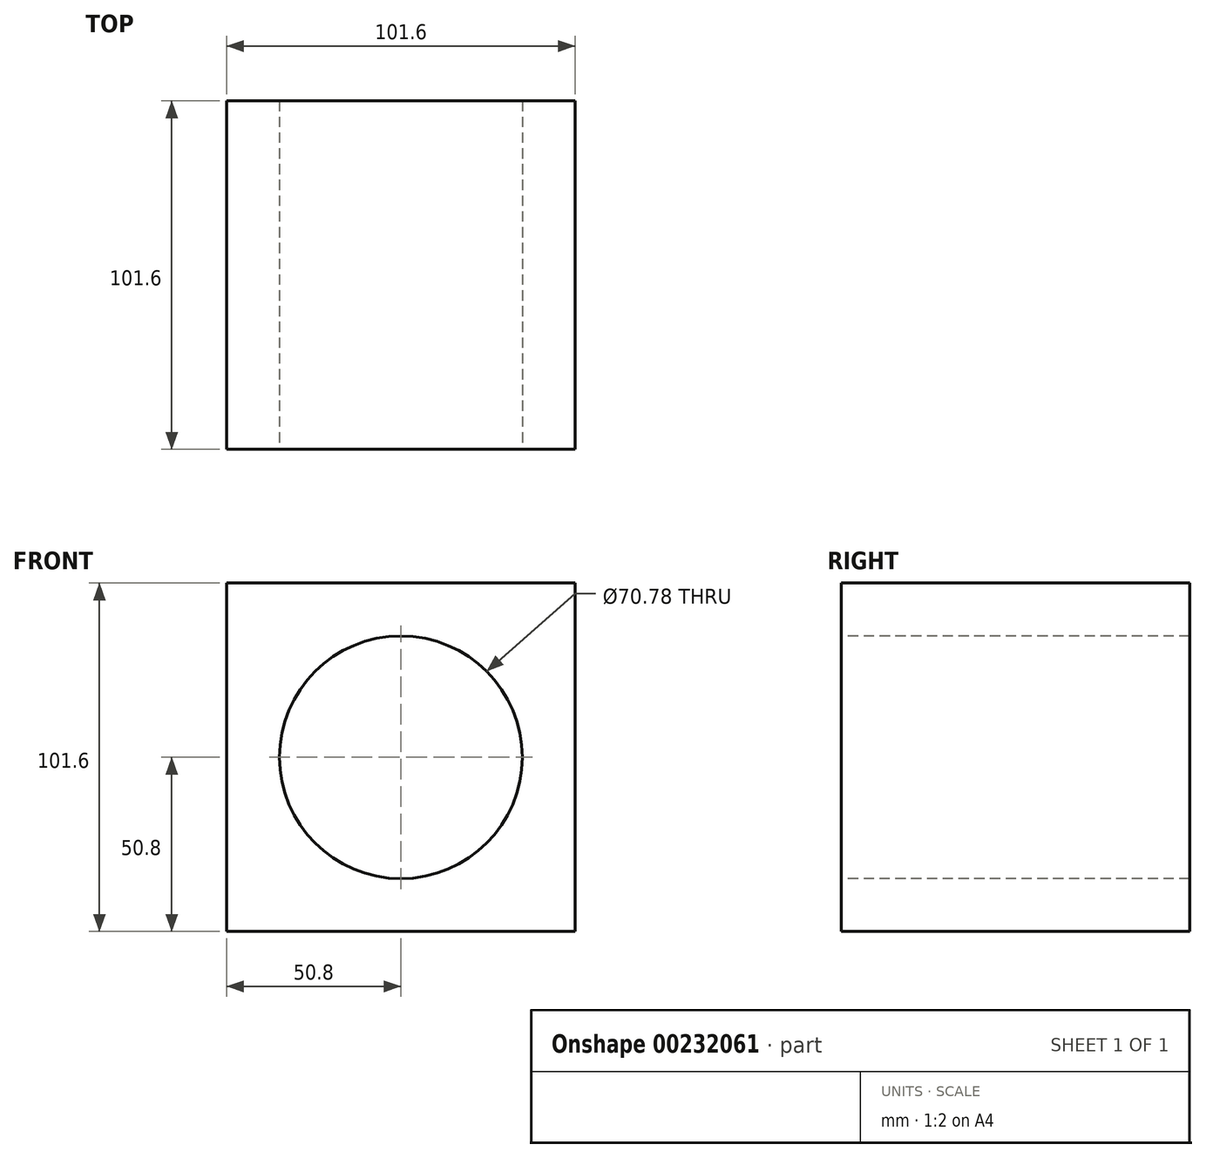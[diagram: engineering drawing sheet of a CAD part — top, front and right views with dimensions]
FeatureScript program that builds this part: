
annotation { "Feature Type Name" : "Feature", "Feature Type Description" : "" }
export const myFeature = defineFeature(function(context is Context, id is Id, definition is map)
    precondition{}
    {
        {
            var Q0;
            Q0=qCreatedBy(makeId("Top.planeOp"),FACE);
            var sketch = newSketch(context, id + "F1", { "sketchPlane" : qUnion([Q0])});
            skLineSegment(sketch, "E0.bottom", {"start": v(50.8, 50.8) * mm, "end": v(-50.8, 50.8) * mm});
            skLineSegment(sketch, "E0.top", {"start": v(50.8, -50.8) * mm, "end": v(-50.8, -50.8) * mm});
            skLineSegment(sketch, "E0.left", {"start": v(50.8, 50.8) * mm, "end": v(50.8, -50.8) * mm});
            skLineSegment(sketch, "E0.right", {"start": v(-50.8, 50.8) * mm, "end": v(-50.8, -50.8) * mm});
            skPoint(sketch, "E0.middle", {"position": v(0, 0) * mm});
            skSolve(sketch);
        }
        {
            var Q0;
            Q0 = qSketchRegion(id + "F1", true);
            extrude(context, id + "F2", {"entities" : qUnion([Q0]), "depth" : 101.6 * mm});
        }
        {
            var Q0;
            Q0=makeQuery(id+"F2.opExtrude","SWEPT_FACE",FACE,{"disambiguationData":[OSD([sQuery(id+"F1.wireOp",EDGE,"E0.top")])]});
            var sketch = newSketch(context, id + "F3", { "sketchPlane" : qUnion([Q0])});
            skCircle(sketch, "E1", {"center": v(0, 50.8) * mm, "radius": 35.39 * mm});
            skPoint(sketch, "E1.centerSnap0", {"position": v(50.8, 50.8) * mm});
            skPoint(sketch, "E1.centerSnap1", {"position": v(0, 101.6) * mm});
            skSolve(sketch);
        }
        {
            var Q0;
            Q0 = qSketchRegion(id + "F3", true);
            extrude(context, id + "F0", {"entities" : qUnion([Q0]), "operationType" : NewBodyOperationType.REMOVE, "oppositeDirection" : true, "depth" : 127 * mm});
        }
    });
